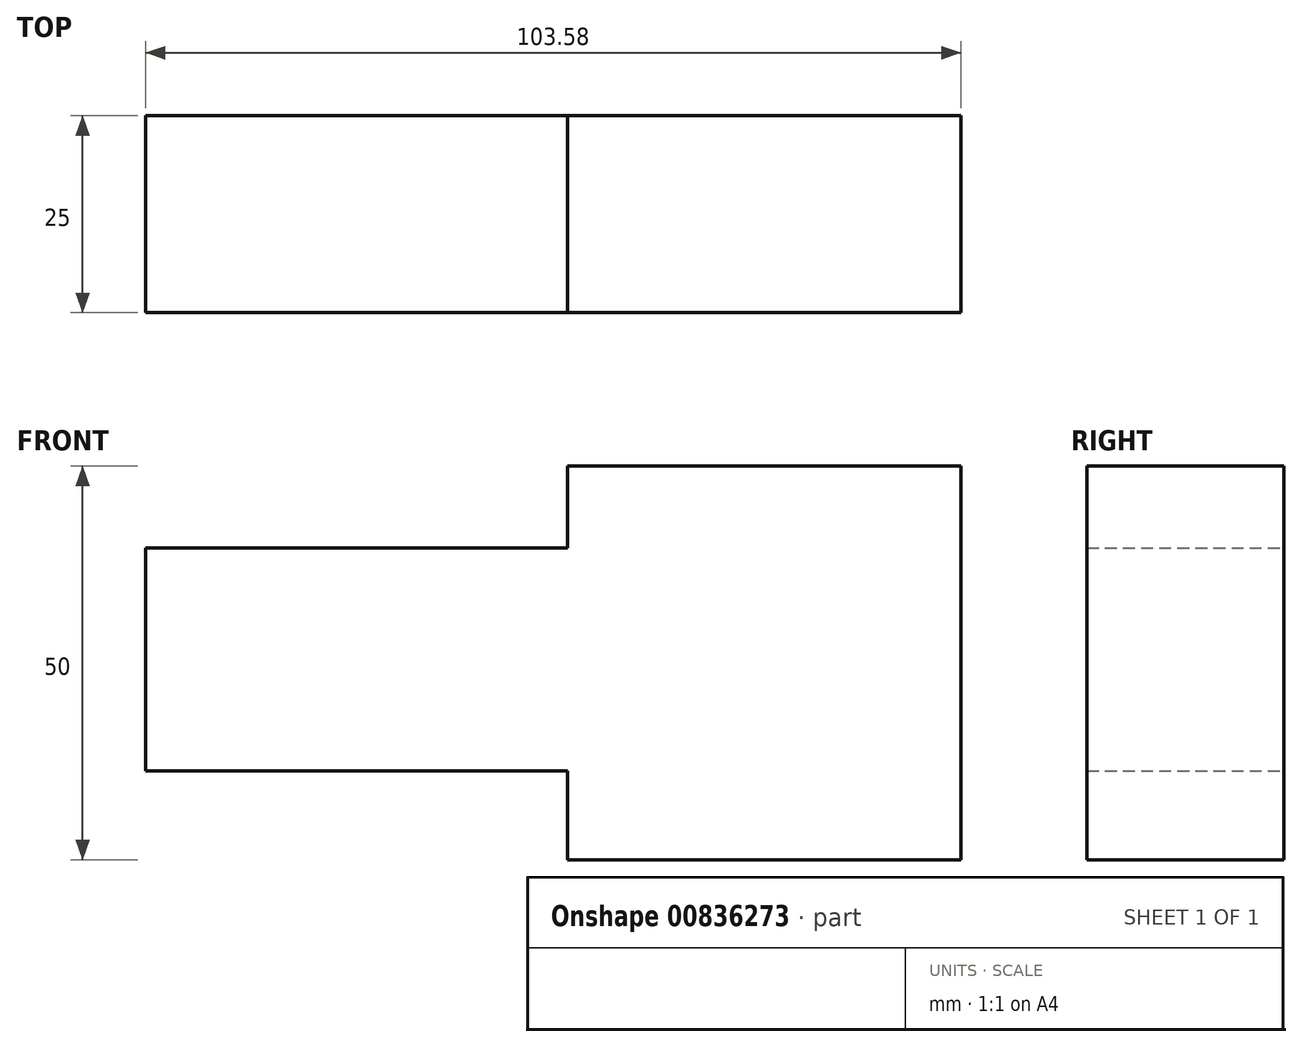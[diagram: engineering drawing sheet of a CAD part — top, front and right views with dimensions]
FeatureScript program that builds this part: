
annotation { "Feature Type Name" : "Feature", "Feature Type Description" : "" }
export const myFeature = defineFeature(function(context is Context, id is Id, definition is map)
    precondition{}
    {
        {
            var Q0;
            Q0=qCreatedBy(makeId("Front.planeOp"),FACE);
            var sketch = newSketch(context, id + "F0", { "sketchPlane" : qUnion([Q0])});
            skLineSegment(sketch, "E0.bottom", {"start": v(-21.21, 27.46) * mm, "end": v(28.79, 27.46) * mm});
            skLineSegment(sketch, "E0.top", {"start": v(-21.21, -22.54) * mm, "end": v(28.79, -22.54) * mm});
            skLineSegment(sketch, "E0.left", {"start": v(-21.21, 27.46) * mm, "end": v(-21.21, -22.54) * mm});
            skLineSegment(sketch, "E0.right", {"start": v(28.79, 27.46) * mm, "end": v(28.79, -22.54) * mm});
            skLineSegment(sketch, "E1.bottom", {"start": v(-74.79, 17.06) * mm, "end": v(-54.07, 17.06) * mm});
            skLineSegment(sketch, "E1.top", {"start": v(-74.79, -11.27) * mm, "end": v(-54.07, -11.27) * mm});
            skLineSegment(sketch, "E1.left", {"start": v(-74.79, 17.06) * mm, "end": v(-74.79, -11.27) * mm});
            skLineSegment(sketch, "E1.right", {"start": v(-54.07, 17.06) * mm, "end": v(-54.07, -11.27) * mm});
            skSolve(sketch);
        }
        {
            var Q0;
            Q0=makeQuery(id+"F0.imprint","IMPRINT",FACE,{"disambiguationData":[TD([[makeQuery(id+"F0.imprint","IMPRINT",EDGE,{"derivedFrom":sQuery(id+"F0.wireOp",EDGE,"E0.bottom")}),-1.0]])]});
            var Q1;
            Q1=makeQuery(id+"F0.imprint","IMPRINT",FACE,{"disambiguationData":[TD([[makeQuery(id+"F0.imprint","IMPRINT",EDGE,{"derivedFrom":sQuery(id+"F0.wireOp",EDGE,"E1.bottom")}),-1.0]])]});
            extrude(context, id + "F1", {"entities" : qUnion([Q0, Q1]), "depth" : 25 * mm, "offsetDistance" : 25 * mm});
        }
        {
            var Q0;
            Q0=makeQuery(id+"F1.opExtrude","SWEPT_FACE",FACE,{"disambiguationData":[OSD([sQuery(id+"F0.wireOp",EDGE,"E1.right")])]});
            extrude(context, id + "F2", {"entities" : qUnion([Q0]), "operationType" : NewBodyOperationType.ADD, "endBound" : BoundingType.UP_TO_NEXT, "depth" : mm, "offsetDistance" : 25 * mm});
        }
    });
